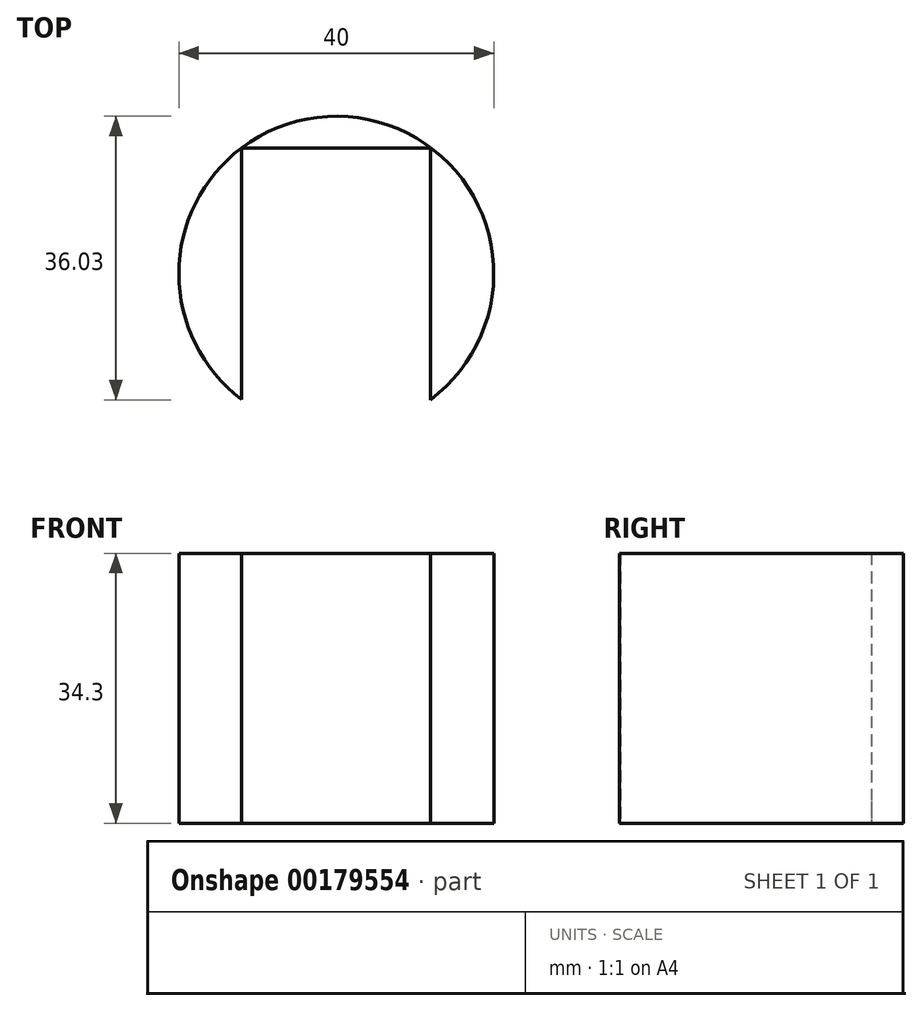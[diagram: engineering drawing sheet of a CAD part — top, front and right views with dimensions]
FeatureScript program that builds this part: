
annotation { "Feature Type Name" : "Feature", "Feature Type Description" : "" }
export const myFeature = defineFeature(function(context is Context, id is Id, definition is map)
    precondition{}
    {
        {
            var Q0;
            Q0=qCreatedBy(makeId("Top.planeOp"),FACE);
            var sketch = newSketch(context, id + "F0", { "sketchPlane" : qUnion([Q0])});
            skCircle(sketch, "E0", {"center": v(-28.43, 6.08) * mm, "radius": 22.97 * mm});
            skCircle(sketch, "E1", {"center": v(-28.43, 6.08) * mm, "radius": 20 * mm});
            skLineSegment(sketch, "E2.bottom", {"start": v(-40.48, 22.05) * mm, "end": v(-16.47, 22.05) * mm});
            skLineSegment(sketch, "E2.top", {"start": v(-40.48, -9.96) * mm, "end": v(-16.47, -9.96) * mm});
            skLineSegment(sketch, "E2.left", {"start": v(-40.48, 22.05) * mm, "end": v(-40.48, -9.96) * mm});
            skLineSegment(sketch, "E2.right", {"start": v(-16.47, 22.05) * mm, "end": v(-16.47, -9.96) * mm});
            skSolve(sketch);
        }
        {
            var Q0;
            {var subQ1=sQuery(id+"F0.wireOp",EDGE,"E2.bottom");Q0=makeQuery(id+"F0.imprint","IMPRINT",FACE,{"disambiguationData":[TD([[makeQuery(id+"F0.imprint","IMPRINT",EDGE,{"derivedFrom":subQ1}),-1.0]])]});}
            extrude(context, id + "F1", {"entities" : qUnion([Q0]), "depth" : 2.8 * mm});
        }
        {
            var Q0;
            Q0=sQuery(id+"F0.wireOp",EDGE,"E0");
            extrude(context, id + "F2", {"bodyType" : ToolBodyType.SURFACE, "surfaceEntities" : qUnion([Q0]), "depth" : 8.13 * mm});
        }
        {
            var Q0;
            Q0=sQuery(id+"F0.wireOp",EDGE,"E1");
            var Q1;
            Q1=sQuery(id+"F0.wireOp",EDGE,"E0");
            extrude(context, id + "F3", {"bodyType" : ToolBodyType.SURFACE, "surfaceEntities" : qUnion([Q0, Q1]), "depth" : 17.78 * mm});
        }
        {
            var Q0;
            {var subQ0=sQuery(id+"F0.wireOp",EDGE,"E2.left");var subQ1=sQuery(id+"F0.wireOp",EDGE,"E1");var subQ3=makeQuery(id+"F0.imprint","INTERSECT",VERTEX,{"derivedFrom":[subQ1,subQ0]});Q0=makeQuery(id+"F0.imprint","IMPRINT",FACE,{"disambiguationData":[TD([[makeQuery(id+"F0.imprint","IMPRINT",EDGE,{"disambiguationData":[TD([[subQ3,1.0]])],"derivedFrom":subQ1}),1.0]])]});}
            var Q1;
            {var subQ0=sQuery(id+"F0.wireOp",EDGE,"E2.bottom");Q1=makeQuery(id+"F0.imprint","IMPRINT",FACE,{"disambiguationData":[TD([[makeQuery(id+"F0.imprint","IMPRINT",EDGE,{"derivedFrom":subQ0}),1.0]])]});}
            extrude(context, id + "F4", {"entities" : qUnion([Q0, Q1]), "operationType" : NewBodyOperationType.ADD, "depth" : 34.3 * mm});
        }
        {
            var Q0;
            {var subQ0=sQuery(id+"F0.wireOp",EDGE,"E2.left");var subQ1=sQuery(id+"F0.wireOp",EDGE,"E1");var subQ3=makeQuery(id+"F0.imprint","INTERSECT",VERTEX,{"derivedFrom":[subQ1,subQ0]});Q0=makeQuery(id+"F0.imprint","IMPRINT",FACE,{"disambiguationData":[TD([[makeQuery(id+"F0.imprint","IMPRINT",EDGE,{"disambiguationData":[TD([[subQ3,1.0]])],"derivedFrom":subQ1}),1.0]])]});}
            extrude(context, id + "F5", {"entities" : qUnion([Q0]), "operationType" : NewBodyOperationType.ADD, "depth" : 25.4 * mm});
        }
        {
            var Q0;
            Q0=makeQuery(id+"F3.opExtrude","SWEPT_BODY",BODY,{"disambiguationData":[OSD([sQuery(id+"F0.wireOp",EDGE,"E1")])]});
            var Q1;
            Q1=makeQuery(id+"F3.opExtrude","SWEPT_BODY",BODY,{"disambiguationData":[OSD([sQuery(id+"F0.wireOp",EDGE,"E0")])]});
            var Q2;
            Q2=makeQuery(id+"F2.opExtrude","SWEPT_BODY",BODY,{"disambiguationData":[OSD([sQuery(id+"F0.wireOp",EDGE,"E0")])]});
            deleteBodies(context, id + "F6", {"entities" : qUnion([Q0, Q1, Q2])});
        }
    });
